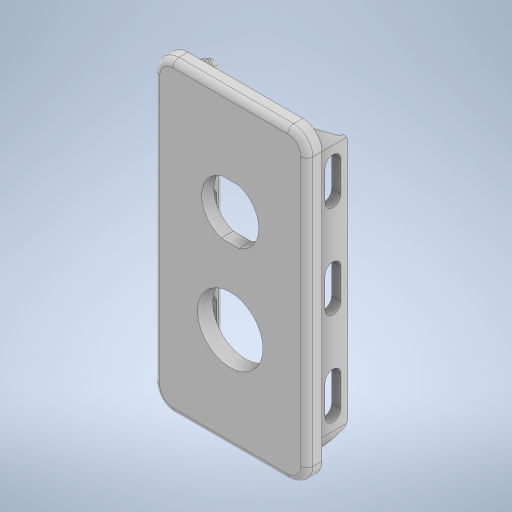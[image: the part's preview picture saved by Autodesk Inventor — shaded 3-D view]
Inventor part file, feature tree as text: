
AUTODESK INVENTOR PART (.ipt)
format: ipt  version: 2023 (Build 270158000, 158)  size: 610,816 bytes
history: native  units: mm
features: extrude x8, sketch x8, fillet x3, plane x2, mirror x1, chamfer x1
ambient origin geometry x8: Origin, YZ Plane, XZ Plane, XY Plane, X Axis, Y Axis, Z Axis, Center Point
bodies: Solid1 (feature_tree)
feature tree (23):
  extrude  "Extrusion1"  Depth=50.8mm
  fillet  "Fillet1"  Radius=6.35mm
  sketch  "Sketch3"  dims[d6=3.375mm d7=6.35mm]
  sketch  "Sketch2"  dims[d3=5.0mm d4=0.0mm d5=2.0mm]
  sketch  "Sketch4"  dims[d8=21.705mm d9=33.866667mm]
  extrude  "Extrusion2"  Depth=2.0mm
  extrude  "Extrusion3"  Depth=6.35mm
  extrude  "Extrusion4"  Depth=33.866667mm
  extrude  "Extrusion5"  Depth=18.95mm
  extrude  "Extrusion6"  Depth=3.0mm
  extrude  "Extrusion7"  Depth=12.0mm TaperAngle=0.0deg
  extrude  "Extrusion8"  Depth=27.6mm
  plane  "Work Plane1"
  mirror  "Mirror1"
  chamfer  "Chamfer2"  Distance=10.0mm
  fillet  "Fillet2"  Radius=25.75mm
  fillet  "Fillet3"  Radius=1.0mm
  sketch  "Sketch1"  dims[d0=101.6mm d1=50.8mm d2=6.35mm]
  sketch  "Sketch5"  dims[d10=33.866667mm d11=18.95mm]
  sketch  "Sketch6"  dims[d13=18.0mm d14=3.0mm]
  sketch  "Sketch7"  dims[d15=3.0mm d16=12.0mm d17=0.0mm]
  sketch  "Sketch8"  dims[d18=3.0mm d19=0.0mm d20=27.6mm d21=10.0mm d22=0.0mm d23=25.75mm d24=1.0mm d25=0.0mm d29=2.613mm d30=7.0mm d31=2.613mm d32=20.0mm d33=20.0mm d34=2.613mm d35=10.0mm d36=0.0mm d37=0.0mm d38=2.613mm d39=10.0mm d40=7.0mm d41=0.0mm d42=0.0mm d43=1.0mm d44=0.0mm d45=2.0mm d46=2.0mm d47=2.5mm d48=2.0mm d49=45.0deg]
  plane  "Work Plane2"
